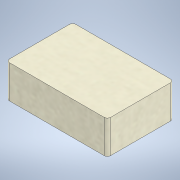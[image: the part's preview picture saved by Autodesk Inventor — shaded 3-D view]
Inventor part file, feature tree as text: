
AUTODESK INVENTOR PART (.ipt)
format: ipt  version: 2021 (Build 250183000, 183)  size: 118,272 bytes
history: native  units: mm
features: extrude x1, sketch x1
ambient origin geometry x8: Origin, YZ Plane, XZ Plane, XY Plane, X Axis, Y Axis, Z Axis, Center Point
bodies: Solid1 (feature_tree)
feature tree (2):
  extrude  "Extrusion1"  Depth=42.0mm
  sketch  "Sketch1"  dims[d0=64.0mm d1=42.0mm d2=2.0mm d3=21.0mm d4=0.0mm]
